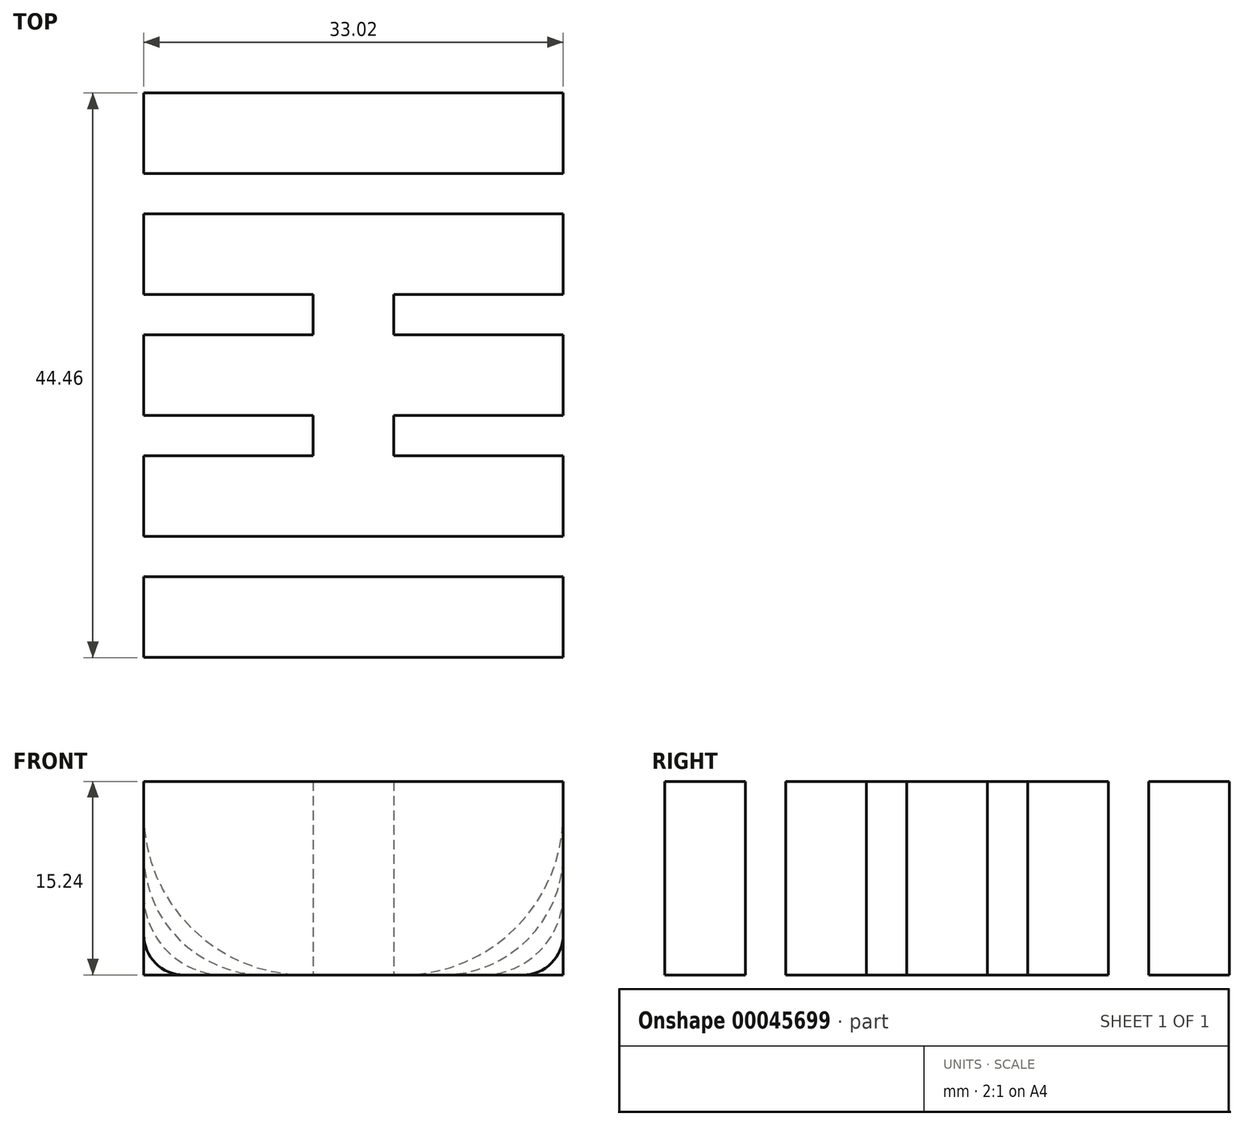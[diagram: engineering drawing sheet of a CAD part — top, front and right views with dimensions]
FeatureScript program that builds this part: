
annotation { "Feature Type Name" : "Feature", "Feature Type Description" : "" }
export const myFeature = defineFeature(function(context is Context, id is Id, definition is map)
    precondition{}
    {
        {
            var Q0;
            Q0=qCreatedBy(makeId("Top.planeOp"),FACE);
            var sketch = newSketch(context, id + "F0", { "sketchPlane" : qUnion([Q0])});
            skLineSegment(sketch, "E0.bottom", {"start": v(-16.51, 3.18) * mm, "end": v(16.51, 3.18) * mm});
            skLineSegment(sketch, "E0.top", {"start": v(-16.51, -3.17) * mm, "end": v(16.51, -3.17) * mm});
            skLineSegment(sketch, "E0.left", {"start": v(-16.51, 3.17) * mm, "end": v(-16.51, -3.18) * mm});
            skLineSegment(sketch, "E0.right", {"start": v(16.51, 3.17) * mm, "end": v(16.51, -3.18) * mm});
            skLineSegment(sketch, "E1", {"start": v(-16.51, 3.18) * mm, "end": v(16.51, -3.18) * mm, "construction": true});
            skLineSegment(sketch, "E2.0.1.0", {"start": v(-16.51, 12.7) * mm, "end": v(16.51, 12.7) * mm});
            skLineSegment(sketch, "E2.0.1.1", {"start": v(-16.51, 6.35) * mm, "end": v(16.51, 6.35) * mm});
            skLineSegment(sketch, "E2.0.1.2", {"start": v(-16.51, 12.7) * mm, "end": v(-16.51, 6.35) * mm});
            skLineSegment(sketch, "E2.0.1.3", {"start": v(16.51, 12.7) * mm, "end": v(16.51, 6.35) * mm});
            skLineSegment(sketch, "E2.0.1.4", {"start": v(-16.51, 12.7) * mm, "end": v(16.51, 6.35) * mm, "construction": true});
            skLineSegment(sketch, "E2.0.2.0", {"start": v(-16.51, 22.23) * mm, "end": v(16.51, 22.23) * mm});
            skLineSegment(sketch, "E2.0.2.1", {"start": v(-16.51, 15.88) * mm, "end": v(16.51, 15.88) * mm});
            skLineSegment(sketch, "E2.0.2.2", {"start": v(-16.51, 22.22) * mm, "end": v(-16.51, 15.88) * mm});
            skLineSegment(sketch, "E2.0.2.3", {"start": v(16.51, 22.22) * mm, "end": v(16.51, 15.88) * mm});
            skLineSegment(sketch, "E2.0.2.4", {"start": v(-16.51, 22.22) * mm, "end": v(16.51, 15.87) * mm, "construction": true});
            skLineSegment(sketch, "E2.direction1", {"start": v(-16.51, 3.18) * mm, "end": v(9.52, 3.18) * mm, "construction": true});
            skLineSegment(sketch, "E2.direction2", {"start": v(-16.51, 3.17) * mm, "end": v(-16.51, 12.7) * mm, "construction": true});
            skLineSegment(sketch, "E3.MirrorCS", {"start": v(-16.51, -22.22) * mm, "end": v(-16.51, -15.88) * mm});
            skLineSegment(sketch, "E4.MirrorCS", {"start": v(-16.51, -15.88) * mm, "end": v(16.51, -15.88) * mm});
            skLineSegment(sketch, "E5.MirrorCS", {"start": v(-16.51, -22.23) * mm, "end": v(16.51, -22.23) * mm});
            skLineSegment(sketch, "E6.MirrorCS", {"start": v(-16.51, -22.22) * mm, "end": v(16.51, -15.87) * mm});
            skLineSegment(sketch, "E7.MirrorCS", {"start": v(-16.51, -12.7) * mm, "end": v(16.51, -6.35) * mm});
            skLineSegment(sketch, "E8.MirrorCS", {"start": v(16.51, -12.7) * mm, "end": v(16.51, -6.35) * mm});
            skLineSegment(sketch, "E9.MirrorCS", {"start": v(-16.51, -12.7) * mm, "end": v(-16.51, -6.35) * mm});
            skLineSegment(sketch, "E10.MirrorCS", {"start": v(-16.51, -6.35) * mm, "end": v(16.51, -6.35) * mm});
            skLineSegment(sketch, "E11.MirrorCS", {"start": v(-16.51, -12.7) * mm, "end": v(16.51, -12.7) * mm});
            skLineSegment(sketch, "E12.MirrorCS", {"start": v(16.51, -22.22) * mm, "end": v(16.51, -15.88) * mm});
            skLineSegment(sketch, "E13.bottom", {"start": v(-3.17, 15.88) * mm, "end": v(3.18, 15.88) * mm});
            skLineSegment(sketch, "E13.top", {"start": v(-3.17, -15.88) * mm, "end": v(3.18, -15.88) * mm});
            skLineSegment(sketch, "E13.left", {"start": v(-3.18, 15.88) * mm, "end": v(-3.17, -15.88) * mm});
            skLineSegment(sketch, "E13.right", {"start": v(3.17, 15.88) * mm, "end": v(3.18, -15.88) * mm});
            skLineSegment(sketch, "E14", {"start": v(3.17, 15.88) * mm, "end": v(-3.18, -15.88) * mm, "construction": true});
            skSolve(sketch);
        }
        {
            var Q0;
            Q0=makeQuery(id+"F0.imprint","IMPRINT",FACE,{"disambiguationData":[TD([[makeQuery(id+"F0.imprint","IMPRINT",EDGE,{"derivedFrom":sQuery(id+"F0.wireOp",EDGE,"E2.0.2.0")}),-1.0]])]});
            var Q1;
            {var subQ4=sQuery(id+"F0.wireOp",EDGE,"E13.bottom");Q1=makeQuery(id+"F0.imprint","IMPRINT",FACE,{"disambiguationData":[TD([[makeQuery(id+"F0.imprint","IMPRINT",EDGE,{"derivedFrom":subQ4}),-1.0]])]});}
            var Q2;
            {var subQ3=sQuery(id+"F0.wireOp",EDGE,"E2.0.1.0");var subQ5=sQuery(id+"F0.wireOp",EDGE,"E13.left");var subQ7=makeQuery(id+"F0.imprint","INTERSECT",VERTEX,{"derivedFrom":[subQ3,subQ5]});Q2=makeQuery(id+"F0.imprint","IMPRINT",FACE,{"disambiguationData":[TD([[makeQuery(id+"F0.imprint","IMPRINT",EDGE,{"disambiguationData":[TD([[subQ7,-1.0]])],"derivedFrom":subQ3}),-1.0]])]});}
            var Q3;
            {var subQ0=sQuery(id+"F0.wireOp",EDGE,"E2.0.1.2");Q3=makeQuery(id+"F0.imprint","IMPRINT",FACE,{"disambiguationData":[TD([[makeQuery(id+"F0.imprint","IMPRINT",EDGE,{"derivedFrom":subQ0}),1.0]])]});}
            var Q4;
            {var subQ5=sQuery(id+"F0.wireOp",EDGE,"E2.0.1.3");Q4=makeQuery(id+"F0.imprint","IMPRINT",FACE,{"disambiguationData":[TD([[makeQuery(id+"F0.imprint","IMPRINT",EDGE,{"derivedFrom":subQ5}),-1.0]])]});}
            var Q5;
            {var subQ3=sQuery(id+"F0.wireOp",EDGE,"E0.bottom");var subQ5=sQuery(id+"F0.wireOp",EDGE,"E13.left");var subQ7=makeQuery(id+"F0.imprint","INTERSECT",VERTEX,{"derivedFrom":[subQ3,subQ5]});Q5=makeQuery(id+"F0.imprint","IMPRINT",FACE,{"disambiguationData":[TD([[makeQuery(id+"F0.imprint","IMPRINT",EDGE,{"disambiguationData":[TD([[subQ7,-1.0]])],"derivedFrom":subQ3}),1.0]])]});}
            var Q6;
            {var subQ0=sQuery(id+"F0.wireOp",EDGE,"E13.left");var subQ3=sQuery(id+"F0.wireOp",EDGE,"E0.bottom");var subQ4=makeQuery(id+"F0.imprint","INTERSECT",VERTEX,{"derivedFrom":[subQ3,subQ0]});Q6=makeQuery(id+"F0.imprint","IMPRINT",FACE,{"disambiguationData":[TD([[makeQuery(id+"F0.imprint","IMPRINT",EDGE,{"disambiguationData":[TD([[subQ4,-1.0]])],"derivedFrom":subQ3}),-1.0]])]});}
            var Q7;
            {var subQ5=sQuery(id+"F0.wireOp",EDGE,"E0.right");Q7=makeQuery(id+"F0.imprint","IMPRINT",FACE,{"disambiguationData":[TD([[makeQuery(id+"F0.imprint","IMPRINT",EDGE,{"derivedFrom":subQ5}),-1.0]])]});}
            var Q8;
            {var subQ5=sQuery(id+"F0.wireOp",EDGE,"E0.left");Q8=makeQuery(id+"F0.imprint","IMPRINT",FACE,{"disambiguationData":[TD([[makeQuery(id+"F0.imprint","IMPRINT",EDGE,{"derivedFrom":subQ5}),1.0]])]});}
            var Q9;
            {var subQ0=sQuery(id+"F0.wireOp",EDGE,"E13.left");var subQ3=sQuery(id+"F0.wireOp",EDGE,"E0.top");var subQ4=makeQuery(id+"F0.imprint","INTERSECT",VERTEX,{"derivedFrom":[subQ3,subQ0]});Q9=makeQuery(id+"F0.imprint","IMPRINT",FACE,{"disambiguationData":[TD([[makeQuery(id+"F0.imprint","IMPRINT",EDGE,{"disambiguationData":[TD([[subQ4,-1.0]])],"derivedFrom":subQ3}),-1.0]])]});}
            var Q10;
            {var subQ3=sQuery(id+"F0.wireOp",EDGE,"E9.MirrorCS");Q10=makeQuery(id+"F0.imprint","IMPRINT",FACE,{"disambiguationData":[TD([[makeQuery(id+"F0.imprint","IMPRINT",EDGE,{"derivedFrom":subQ3}),-1.0]])]});}
            var Q11;
            {var subQ1=sQuery(id+"F0.wireOp",EDGE,"E7.MirrorCS");var subQ5=sQuery(id+"F0.wireOp",EDGE,"E13.left");var subQ7=makeQuery(id+"F0.imprint","INTERSECT",VERTEX,{"derivedFrom":[subQ1,subQ5]});Q11=makeQuery(id+"F0.imprint","IMPRINT",FACE,{"disambiguationData":[TD([[makeQuery(id+"F0.imprint","IMPRINT",EDGE,{"disambiguationData":[TD([[subQ7,-1.0]])],"derivedFrom":subQ1}),1.0]])]});}
            var Q12;
            {var subQ5=sQuery(id+"F0.wireOp",EDGE,"E8.MirrorCS");Q12=makeQuery(id+"F0.imprint","IMPRINT",FACE,{"disambiguationData":[TD([[makeQuery(id+"F0.imprint","IMPRINT",EDGE,{"derivedFrom":subQ5}),1.0]])]});}
            var Q13;
            {var subQ4=sQuery(id+"F0.wireOp",EDGE,"E13.top");Q13=makeQuery(id+"F0.imprint","IMPRINT",FACE,{"disambiguationData":[TD([[makeQuery(id+"F0.imprint","IMPRINT",EDGE,{"derivedFrom":subQ4}),1.0]])]});}
            var Q14;
            {var subQ0=sQuery(id+"F0.wireOp",EDGE,"E3.MirrorCS");Q14=makeQuery(id+"F0.imprint","IMPRINT",FACE,{"disambiguationData":[TD([[makeQuery(id+"F0.imprint","IMPRINT",EDGE,{"derivedFrom":subQ0}),-1.0]])]});}
            var Q15;
            {var subQ1=sQuery(id+"F0.wireOp",EDGE,"E7.MirrorCS");var subQ5=sQuery(id+"F0.wireOp",EDGE,"E13.left");var subQ6=makeQuery(id+"F0.imprint","INTERSECT",VERTEX,{"derivedFrom":[subQ1,subQ5]});Q15=makeQuery(id+"F0.imprint","IMPRINT",FACE,{"disambiguationData":[TD([[makeQuery(id+"F0.imprint","IMPRINT",EDGE,{"disambiguationData":[TD([[subQ6,-1.0]])],"derivedFrom":subQ1}),-1.0]])]});}
            var Q16;
            {var subQ0=sQuery(id+"F0.wireOp",EDGE,"E13.left");var subQ3=sQuery(id+"F0.wireOp",EDGE,"E11.MirrorCS");var subQ4=makeQuery(id+"F0.imprint","INTERSECT",VERTEX,{"derivedFrom":[subQ3,subQ0]});Q16=makeQuery(id+"F0.imprint","IMPRINT",FACE,{"disambiguationData":[TD([[makeQuery(id+"F0.imprint","IMPRINT",EDGE,{"disambiguationData":[TD([[subQ4,1.0]])],"derivedFrom":subQ0}),-1.0]])]});}
            var Q17;
            {var subQ0=sQuery(id+"F0.wireOp",EDGE,"E13.right");var subQ3=sQuery(id+"F0.wireOp",EDGE,"E10.MirrorCS");var subQ4=makeQuery(id+"F0.imprint","INTERSECT",VERTEX,{"derivedFrom":[subQ3,subQ0]});Q17=makeQuery(id+"F0.imprint","IMPRINT",FACE,{"disambiguationData":[TD([[makeQuery(id+"F0.imprint","IMPRINT",EDGE,{"disambiguationData":[TD([[subQ4,-1.0]])],"derivedFrom":subQ0}),1.0]])]});}
            var Q18;
            Q18=makeQuery(id+"F0.imprint","IMPRINT",FACE,{"disambiguationData":[TD([[makeQuery(id+"F0.imprint","IMPRINT",EDGE,{"derivedFrom":sQuery(id+"F0.wireOp",EDGE,"E5.MirrorCS")}),1.0]])]});
            extrude(context, id + "F1", {"entities" : qUnion([Q0, Q1, Q2, Q3, Q4, Q5, Q6, Q7, Q8, Q9, Q10, Q11, Q12, Q13, Q14, Q15, Q16, Q17, Q18]), "depth" : 15.24 * mm});
        }
        {
            var Q0;
            Q0=makeQuery(id+"F1.opExtrude","CAP_EDGE",EDGE,{"disambiguationData":[OSD([sQuery(id+"F0.wireOp",EDGE,"E3.MirrorCS")])],"isStart":true});
            var Q1;
            Q1=makeQuery(id+"F1.opExtrude","CAP_EDGE",EDGE,{"disambiguationData":[OSD([sQuery(id+"F0.wireOp",EDGE,"E12.MirrorCS")])],"isStart":true});
            fillet(context, id + "F2", {"entities" : qUnion([Q0, Q1]), "radius" : 3.17 * mm, "tangentPropagation" : true, "allowEdgeOverflow" : false});
        }
        {
            var Q0;
            Q0=makeQuery(id+"F1.opExtrude","CAP_EDGE",EDGE,{"disambiguationData":[OSD([sQuery(id+"F0.wireOp",EDGE,"E9.MirrorCS")])],"isStart":true});
            var Q1;
            Q1=makeQuery(id+"F1.opExtrude","CAP_EDGE",EDGE,{"disambiguationData":[OSD([sQuery(id+"F0.wireOp",EDGE,"E8.MirrorCS")])],"isStart":true});
            fillet(context, id + "F3", {"entities" : qUnion([Q0, Q1]), "radius" : 6.35 * mm, "tangentPropagation" : true, "allowEdgeOverflow" : false});
        }
        {
            var Q0;
            Q0=makeQuery(id+"F1.opExtrude","CAP_EDGE",EDGE,{"disambiguationData":[OSD([sQuery(id+"F0.wireOp",EDGE,"E0.left")])],"isStart":true});
            var Q1;
            Q1=makeQuery(id+"F1.opExtrude","CAP_EDGE",EDGE,{"disambiguationData":[OSD([sQuery(id+"F0.wireOp",EDGE,"E0.right")])],"isStart":true});
            fillet(context, id + "F4", {"entities" : qUnion([Q0, Q1]), "radius" : 9.52 * mm, "tangentPropagation" : true, "allowEdgeOverflow" : false});
        }
        {
            var Q0;
            Q0=makeQuery(id+"F1.opExtrude","CAP_EDGE",EDGE,{"disambiguationData":[OSD([sQuery(id+"F0.wireOp",EDGE,"E2.0.1.3")])],"isStart":true});
            var Q1;
            Q1=makeQuery(id+"F1.opExtrude","CAP_EDGE",EDGE,{"disambiguationData":[OSD([sQuery(id+"F0.wireOp",EDGE,"E2.0.1.2")])],"isStart":true});
            fillet(context, id + "F5", {"entities" : qUnion([Q0, Q1]), "radius" : 12.7 * mm, "tangentPropagation" : true, "allowEdgeOverflow" : false});
        }
        {
            var Q0;
            Q0=qCreatedBy(makeId("Top.planeOp"),FACE);
            var sketch = newSketch(context, id + "F6", { "sketchPlane" : qUnion([Q0])});
            skCircle(sketch, "E15", {"center": v(0, 0) * mm, "radius": 16.02 * mm});
            skSolve(sketch);
        }
    });
